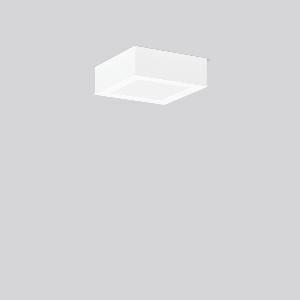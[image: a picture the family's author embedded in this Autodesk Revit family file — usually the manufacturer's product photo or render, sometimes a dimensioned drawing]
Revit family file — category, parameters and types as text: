
# Revit family: toledo_flat_square_a_901552_002_1_76_cbb9
name_source: partatom
category: Lighting Fixtures
units: mm (PartAtom-declared; Revit-internal decimal feet)

## family parameters
Cut with Voids When Loaded = No
Host = Face
Light Source = No
Part Type = Normal
Room Calculation Point = No
Round Connector Dimension = Use Diameter
Shared = No

## types (1)
- TOLEDO FLAT square A (1 x LED Modul 840, 800 lm, 4000)
    Apparent Load = 8 VA
    CIE Flux Codes = 49 80 96 100 100
    Color Rendering = 80
    Color Temperature = 4000
    Default Elevation = 1800 mm
    Description = Series: TOLEDO FLAT square
Ultra thin surface mounted downlight. Surface mounted housing: sheet steel, powder-coated. Square cover plate: die-cast aluminium, powder coated. Light guide and diffuser made of non-yellowing PMMA, opal matt. Suitable for Ceiling mounting, Wall (surface). Driver integrated. 
Colour: white
Length: 172 mm
Width: 172 mm
Height: 58 mm
Lamp: LED
Socket: without socket
Colour temperature: 4000K
Colour rendering index (CRI): 80
System power: 8 W
Rated luminous flux: 800 lm
Luminous efficiency: 100 lm/W
Control gear: Converter, dimmable, DALI
Protection class: II
Type of protection: IP 40
    Height = 58 mm
    Lamp = 1 x LED Modul 840
    Lamp Light Flux = 800 lm
    Lamp count = 1
    Length = 172 mm
    Lifetime = 50000 h
    Luminous efficacy = 100 lm/W
    Manufacturer = RZB
    ModVariant = No
    Model = 901552.002.1.76
    Mounting Place = Ceiling
    Mounting Type = Surface mounted
    Number of Poles = 1
    OnlyDefault = Yes
    Power Factor = 1
    Product Name = TOLEDO FLAT square A
    Product group = Surface mounted downlights
    ProductGroupID = 302
    Protection Class = Protection class II
    Protection Degree = IP 40
    RLX_Detail_Level = 1
    RLX_Emergency_Light_Flux = 0 lm
    RLX_Emergency_Type = 0
    RLX_Emergency_Type_DB = No
    RlxData = <blob elided: 13673 chars, md5=925f99f1>
    Socket = socket
    Standby Power = 0 W
    System Light Flux = 800 lm
    System Power = 8 W
    Type Comments = Product without accessories
    Type Image = 901552.002.jpg
    URL = http://relux.com
    VarID = ---
    Voltage = 230 V
    Voltage Range = 220-240 V
    Weight = 0.00 kg
    Width = 172 mm

## geometry (parser evidence)
native form markers: Sweep x9
no freeform markers — native parametric forms only
